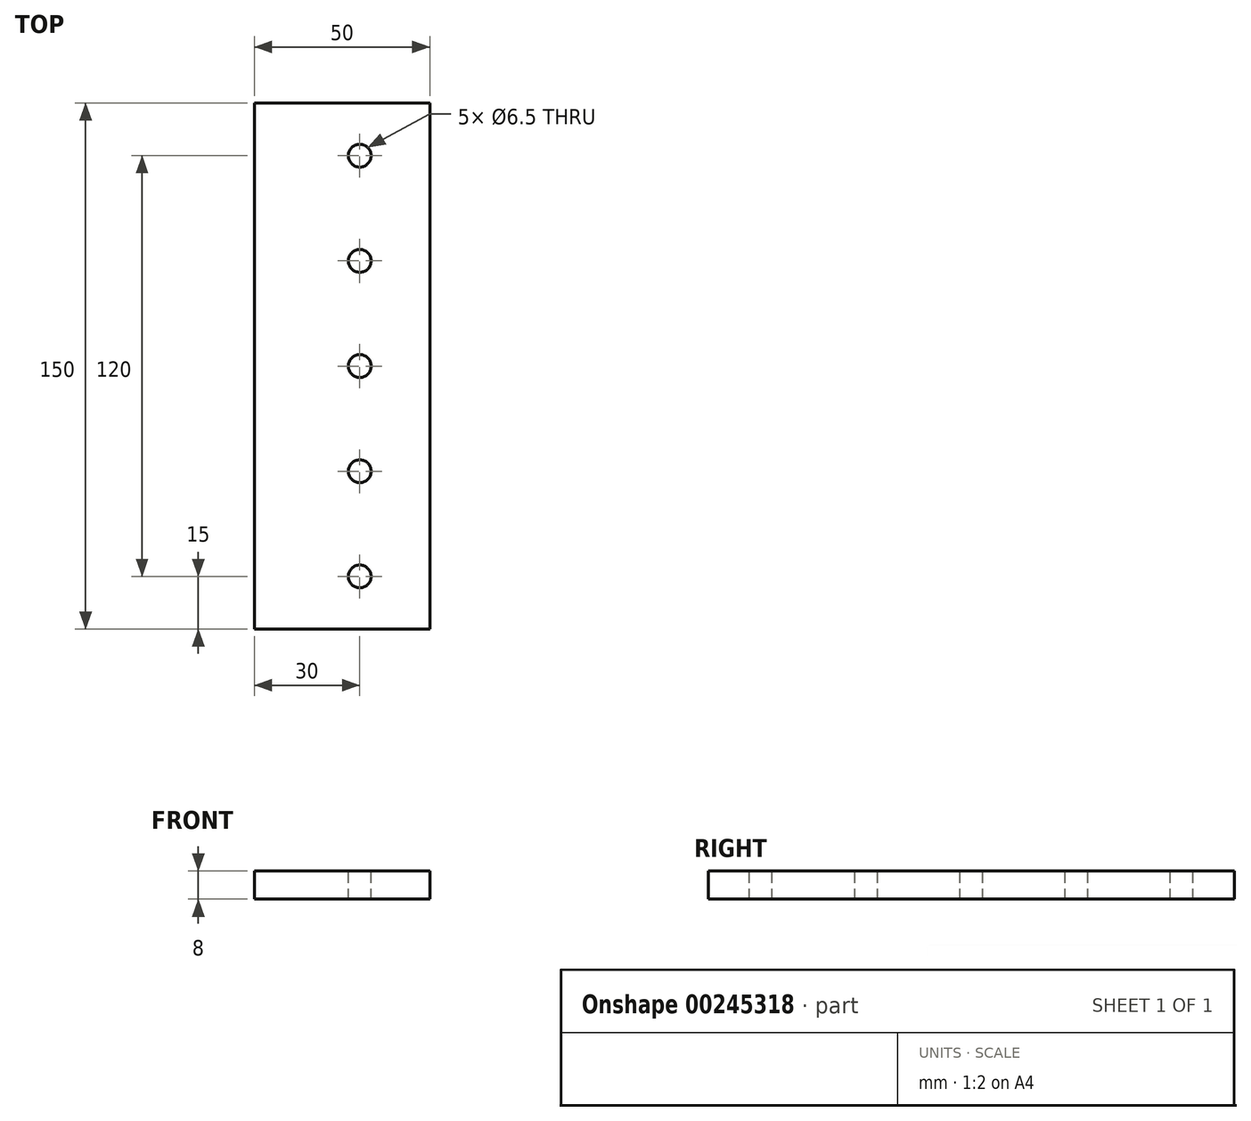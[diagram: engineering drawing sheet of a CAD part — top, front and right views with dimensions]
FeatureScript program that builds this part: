
annotation { "Feature Type Name" : "Feature", "Feature Type Description" : "" }
export const myFeature = defineFeature(function(context is Context, id is Id, definition is map)
    precondition{}
    {
        {
            var Q0;
            Q0=qCreatedBy(makeId("Front.planeOp"),FACE);
            var sketch = newSketch(context, id + "F0", { "sketchPlane" : qUnion([Q0])});
            skLineSegment(sketch, "E0.bottom", {"start": v(0, 0) * mm, "end": v(50, 0) * mm});
            skLineSegment(sketch, "E0.top", {"start": v(0, 8) * mm, "end": v(50, 8) * mm});
            skLineSegment(sketch, "E0.left", {"start": v(0, 0) * mm, "end": v(0, 8) * mm});
            skLineSegment(sketch, "E0.right", {"start": v(50, 0) * mm, "end": v(50, 8) * mm});
            skSolve(sketch);
        }
        {
            var Q0;
            Q0=makeQuery(id+"F0.imprint","IMPRINT",FACE,{"disambiguationData":[TD([[makeQuery(id+"F0.imprint","IMPRINT",EDGE,{"derivedFrom":sQuery(id+"F0.wireOp",EDGE,"E0.bottom")}),1.0]])]});
            extrude(context, id + "F1", {"entities" : qUnion([Q0]), "depth" : 150 * mm});
        }
        {
            var Q0;
            Q0=makeQuery(id+"F1.opExtrude","SWEPT_FACE",FACE,{"disambiguationData":[OSD([sQuery(id+"F0.wireOp",EDGE,"E0.top")])]});
            var sketch = newSketch(context, id + "F2", { "sketchPlane" : qUnion([Q0])});
            skPoint(sketch, "E1", {"position": v(30, -15) * mm});
            skPoint(sketch, "E2", {"position": v(30, -45) * mm});
            skPoint(sketch, "E3", {"position": v(30, -75) * mm});
            skPoint(sketch, "E4", {"position": v(30, -105) * mm});
            skPoint(sketch, "E5", {"position": v(30, -135) * mm});
            skSolve(sketch);
        }
        {
            var Q0;
            Q0=sQuery(id+"F2.wireOp",VERTEX,"E1");
            var Q1;
            Q1=sQuery(id+"F2.wireOp",VERTEX,"E2");
            var Q2;
            Q2=sQuery(id+"F2.wireOp",VERTEX,"E3");
            var Q3;
            Q3=sQuery(id+"F2.wireOp",VERTEX,"E4");
            var Q4;
            Q4=sQuery(id+"F2.wireOp",VERTEX,"E5");
            var Q5;
            Q5=makeQuery(id+"F1.opExtrude","SWEPT_BODY",BODY,{"disambiguationData":[OSD([sQuery(id+"F0.wireOp",EDGE,"E0.bottom"),sQuery(id+"F0.wireOp",EDGE,"E0.top"),sQuery(id+"F0.wireOp",EDGE,"E0.left"),sQuery(id+"F0.wireOp",EDGE,"E0.right")])]});
            hole(context, id + "F3", {"style" : HoleStyle.SIMPLE, "endStyle" : HoleEndStyle.THROUGH, "holeDiameter" : 6.5 * mm, "tappedDepth" : 12 * mm, "tapClearance" : 3, "locations" : qUnion([Q0, Q1, Q2, Q3, Q4]), "scope" : qUnion([Q5])});
        }
    });
